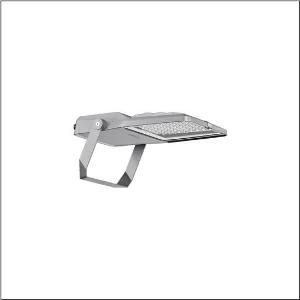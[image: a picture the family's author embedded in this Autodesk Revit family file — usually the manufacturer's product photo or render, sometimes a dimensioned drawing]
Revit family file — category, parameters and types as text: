
# Revit family: floodlight_fl_21_mini___pl61_5xa7776d2c1a_dc0d
name_source: partatom
category: Lighting Fixtures
units: mm (PartAtom-declared; Revit-internal decimal feet)

## family parameters
Cut with Voids When Loaded = No
Host = Face
Light Source = No
Part Type = Normal
Room Calculation Point = No
Round Connector Dimension = Use Diameter
Shared = No

## types (1)
- --- (1 x LED, 17510 lm, 142.9 W, 3000K)
    Apparent Load = 143 VA
    CIE Flux Codes = 33 65 98 100 100
    Color Rendering = 70
    Color Temperature = 3000K
    Default Elevation = 1800 mm
    Description = Floodlight FL 21 mini, floodlight, primary light control with lens, of PMMA, primary optical cover: protective disc, of toughened safety glass, transparent, light distribution: PL61, light emission: direct distribution, installation type: surface-mounted, LED, High Power LED, rated luminous flux: 17.510lm, luminous efficacy: 123lm/W, light colour: 730, colour temperature: 3000K, control: flexible luminous flux parameterisation, time-dependent luminous flux control, constant luminous flux control, overheat protection, presetting dimming logarithmic, with terminal, 6-pole, mains connection: 220..240V, AC, 50/60Hz, start of lifetime: 143W, end of service life: 151W, reduction: 63W, luminaire housing, of diecast aluminium, powder-coated, Siteco® metallic grey (DB 702S), corrosivity category C5 mid according to DIN EN ISO 12944, sealing non-destructively replaceable, mounting bracket, of steel, galvanised, powder-coated, Siteco® metallic grey (DB 702S), Smart Interface below and above, protection rating (complete): IP66, insulation class (complete): insulation class II (safety insulation), certification: CE, ENEC, VDE, protection symbol: D, impact resistance: IK08, permissible operating ambient temperature: -40..+40°C, permissible operating ambient temperature for outdoor applications: -40..+50°C, standard: DIN EN 12944, LABS conformity tested according to VDMA 24364:2018-05, packaging unit: 1 piece

Light Distribution: PL61
    Height = 70 mm
    Lamp = 1 x LED
    Lamp Light Flux = 17510 lm
    Lamp Power = 142.9 W
    Lamp count = 1
    Length = 485 mm
    Luminous efficacy = 123 lm/W
    Manufacturer = Siteco
    ModVariant = No
    Model = 5XA7776D2C1A
    Number of Poles = 1
    OnlyDefault = Yes
    Power Factor = 1
    Product Name = Floodlight FL 21 mini | PL61
    Product group = floodlight | pylon annexe
    ProductGroupID = 6200
    Protection Class = Protection class II
    Protection Degree = IP 66
    RLX_Detail_Level = 1
    RLX_Emergency_Light_Flux = 0 lm
    RLX_Emergency_Type = 0
    RLX_Emergency_Type_DB = No
    RlxData = <blob elided: 96385 chars, md5=bf97377d>
    Socket = socket
    Standby Power = 0 W
    System Light Flux = 17510 lm
    System Power = 143 W
    Type Comments = factory setting: luminous flux: 100 % | dim-lin: 254 | 730 mA
    Type Image = l_1006845.jpg
    URL = http://relux.com
    VarID = @adj_104965
    Voltage = 0 V
    Weight = 0.00 kg
    Width = 337 mm

## geometry (parser evidence)
native form markers: Blend x4, Sweep x12
no freeform markers — native parametric forms only
